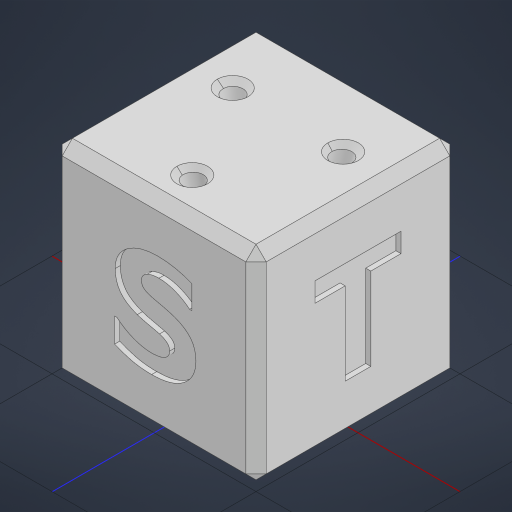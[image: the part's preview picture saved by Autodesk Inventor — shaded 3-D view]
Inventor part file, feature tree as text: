
AUTODESK INVENTOR PART (.ipt)
format: ipt  version: 2023.2 (Build 272271030, 271C)  size: 337,920 bytes
history: native  units: mm
features: sketch x7, other x4, loft x3, chamfer x2, extrude x1, plane x1
ambient origin geometry x8: Origin, YZ Plane, XZ Plane, XY Plane, X Axis, Y Axis, Z Axis, Center Point
bodies: Volumenkörper1 (feature_tree)
feature tree (18):
  extrude  "Extrusion1"  Depth=40.0mm
  plane  "Arbeitsebene2"
  sketch  "Skizze8"  dims[d32=25.0mm]
  sketch  "Skizze9"  dims[d33=4.0mm d34=30.0mm d36=360.0deg d38=15.0mm d39=2.0mm d40=30.0mm d42=360.0deg d44=0.0mm d45=90.0deg d46=0.0mm d47=90.0deg d48=0.0mm d49=90.0deg d50=0.0mm d51=90.0deg d52=0.0mm d53=90.0deg d54=0.0mm d55=90.0deg d56=1.0mm d57=2.0mm d58=45.0deg]
  loft  "Erhebung1"
  loft  "Erhebung2"
  loft  "Erhebung3"
  chamfer  "Fase1"  Distance=30.0mm Angle=360.0deg
  chamfer  "Fase2"  Distance=15.0mm
  sketch  "Skizze4"  dims[d3=0.0mm d18=2.0mm d19=2.0mm d20=45.0deg]
  sketch  "Skizze5"  dims[d23=1.0mm d24=0.0mm d25=1.0mm d26=0.0mm]
  sketch  "Skizze6"  dims[d27=1.0mm d28=0.0mm d29=1.0mm d30=0.0mm]
  sketch  "Skizze7"  dims[d31=-27.0mm]
  other  "Prägen1"
  other  "Prägen2"
  other  "Prägen3"
  other  "Prägen4"
  sketch  "Skizze1"  dims[d0=40.0mm d2=40.0mm]
